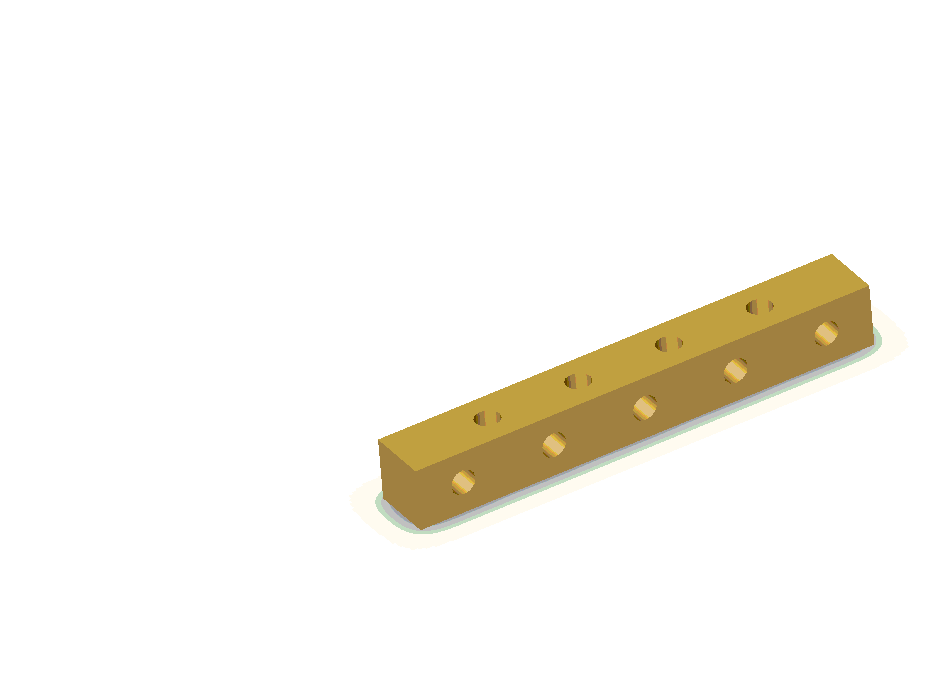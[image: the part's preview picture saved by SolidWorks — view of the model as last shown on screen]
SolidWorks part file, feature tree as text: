
SOLIDWORKS PART (.sldprt)
format: sldprt  version: not decoded by parser v0  size: 114,688 bytes
history: native  units: mm
features: sketch x3, cut_extrude x2, pattern_linear x2, extrude x1 (+8 scaffold rows collapsed)
feature tree (16):
  scaffold x8  (default folders/planes/origin — collapsed)
  sketch  "Sketch1"  dims[D1=12.7mm D2=12.7mm]
  extrude  "Base-Extrude"  Depth=95.25mm
  sketch  "Sketch2"  dims[D3=5.1054mm D1=6.35mm D2=9.525mm]
  cut_extrude  "Cut-Extrude1"  [1 undecoded]
  pattern_linear  "LPattern1"  Count1=5 Count2=1 Spacing1=19.05mm Spacing2=50mm
  sketch  "Sketch3"  dims[D3=5.1054mm D1=19.05mm D2=6.35mm]
  cut_extrude  "Cut-Extrude2"  [1 undecoded]
  pattern_linear  "LPattern2"  Count1=4 Count2=1 Spacing1=19.05mm Spacing2=50mm
decode coverage: 6 of 8 modeling features carry decoded parameters
note: 2 parameter values undecoded
note: suppression state not decoded; provenance and decode notes live in map.json
